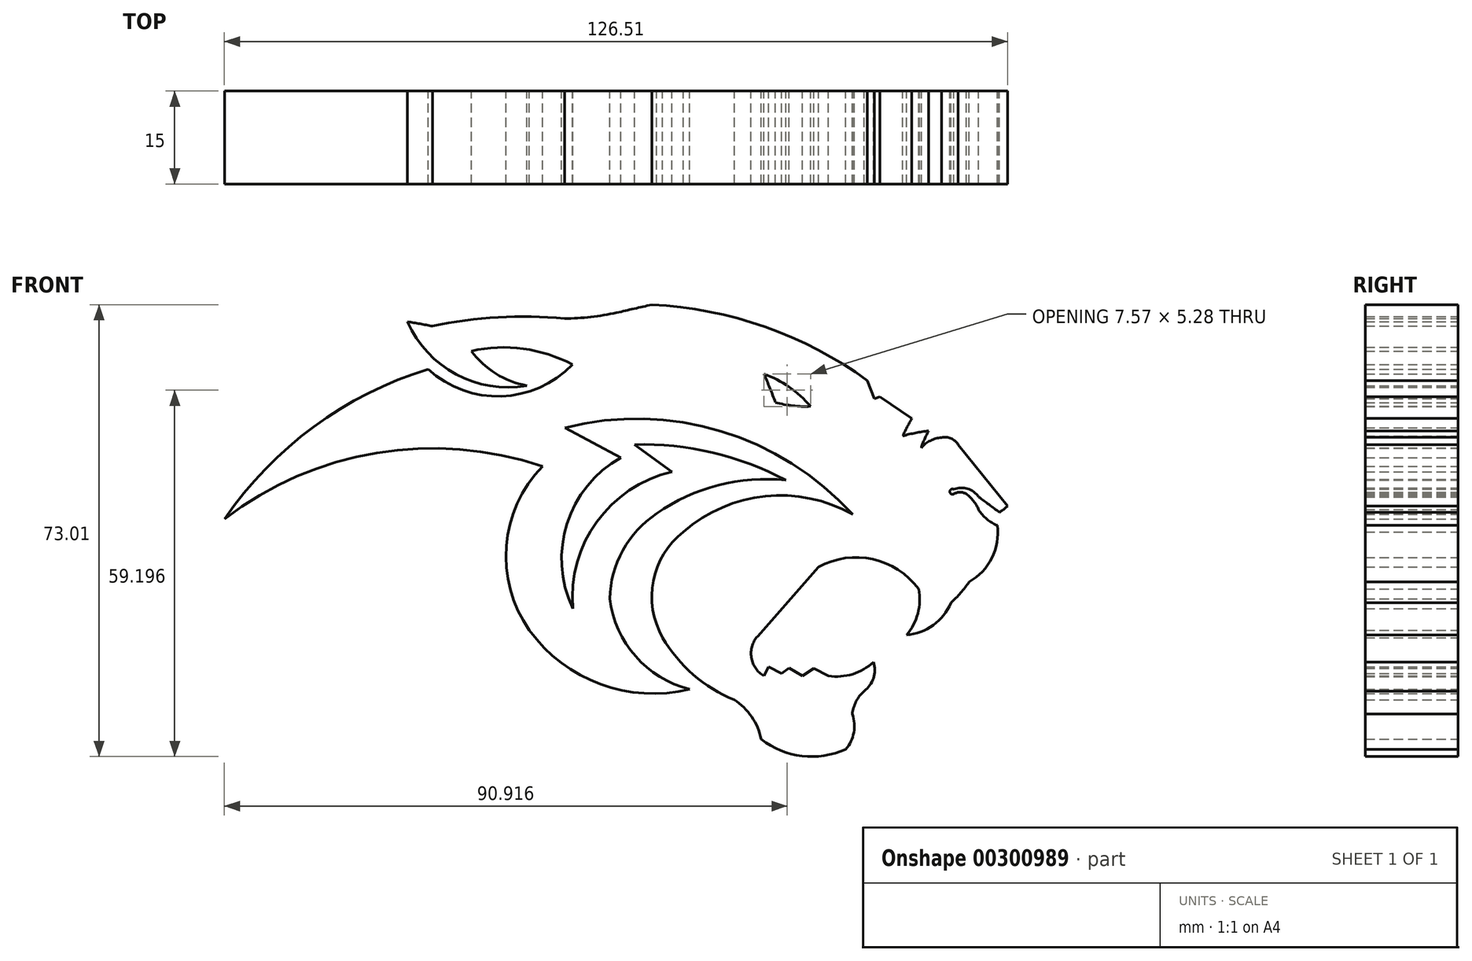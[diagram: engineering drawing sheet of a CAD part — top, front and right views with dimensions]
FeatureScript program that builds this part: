
annotation { "Feature Type Name" : "Feature", "Feature Type Description" : "" }
export const myFeature = defineFeature(function(context is Context, id is Id, definition is map)
    precondition{}
    {
        {
            var Q0;
            Q0=qCreatedBy(makeId("Front.planeOp"),FACE);
            var sketch = newSketch(context, id + "F0", { "sketchPlane" : qUnion([Q0])});
            skArc(sketch, "E0", {"start": v(-29.94, 30.64) * mm, "mid": v(-48.45, 21.32) * mm, "end": v(-62.86, 6.44) * mm});
            skArc(sketch, "E1", {"start": v(-29.94, 30.64) * mm, "mid": v(-18.13, 26.27) * mm, "end": v(-6.62, 31.4) * mm});
            skArc(sketch, "E2", {"start": v(-6.62, 31.4) * mm, "mid": v(-14.6, 33.95) * mm, "end": v(-22.95, 33.58) * mm});
            skArc(sketch, "E3", {"start": v(-22.95, 33.58) * mm, "mid": v(-19, 29.92) * mm, "end": v(-14, 27.98) * mm});
            skArc(sketch, "E4", {"start": v(-33.27, 38.3) * mm, "mid": v(-25.42, 29.8) * mm, "end": v(-14, 27.98) * mm});
            skArc(sketch, "E5", {"start": v(-29.26, 37.6) * mm, "mid": v(-31.26, 37.97) * mm, "end": v(-33.27, 38.3) * mm});
            skArc(sketch, "E6", {"start": v(-7.92, 38.83) * mm, "mid": v(-18.64, 39.04) * mm, "end": v(-29.26, 37.6) * mm});
            skArc(sketch, "E7", {"start": v(-7.92, 38.83) * mm, "mid": v(-3.68, 39.07) * mm, "end": v(0.5, 39.77) * mm});
            skArc(sketch, "E8", {"start": v(0.5, 39.77) * mm, "mid": v(3.34, 40.41) * mm, "end": v(6.17, 41.07) * mm});
            skArc(sketch, "E9", {"start": v(41, 28.8) * mm, "mid": v(24.48, 37.47) * mm, "end": v(6.17, 41.07) * mm});
            skLineSegment(sketch, "E10", {"start": v(41, 28.8) * mm, "end": v(42.13, 25.86) * mm});
            skLineSegment(sketch, "E11", {"start": v(42.13, 25.86) * mm, "end": v(43.05, 26.21) * mm});
            skLineSegment(sketch, "E12", {"start": v(43.05, 26.21) * mm, "end": v(48.2, 22.68) * mm});
            skArc(sketch, "E13", {"start": v(48.2, 22.68) * mm, "mid": v(47.42, 21.29) * mm, "end": v(46.73, 19.85) * mm});
            skArc(sketch, "E14", {"start": v(50.91, 20.67) * mm, "mid": v(48.8, 20.36) * mm, "end": v(46.73, 19.85) * mm});
            skArc(sketch, "E15", {"start": v(50.91, 20.67) * mm, "mid": v(50.25, 19.35) * mm, "end": v(49.73, 17.96) * mm});
            skArc(sketch, "E16", {"start": v(52.98, 19.61) * mm, "mid": v(51.2, 19.1) * mm, "end": v(49.73, 17.96) * mm});
            skArc(sketch, "E17", {"start": v(55.69, 18.43) * mm, "mid": v(54.52, 19.46) * mm, "end": v(52.98, 19.61) * mm});
            skLineSegment(sketch, "E18", {"start": v(55.69, 18.43) * mm, "end": v(63.65, 8.53) * mm});
            skArc(sketch, "E19", {"start": v(62.35, 7.53) * mm, "mid": v(63.03, 8) * mm, "end": v(63.65, 8.53) * mm});
            skArc(sketch, "E20", {"start": v(58.99, 10) * mm, "mid": v(60.67, 8.76) * mm, "end": v(62.35, 7.53) * mm});
            skArc(sketch, "E21", {"start": v(58.99, 10) * mm, "mid": v(57.2, 11.34) * mm, "end": v(54.98, 11.24) * mm});
            skArc(sketch, "E22", {"start": v(54.98, 11.24) * mm, "mid": v(54.32, 10.86) * mm, "end": v(54.98, 10.47) * mm});
            skArc(sketch, "E23", {"start": v(56.99, 10.47) * mm, "mid": v(55.98, 10.77) * mm, "end": v(54.98, 10.47) * mm});
            skArc(sketch, "E24", {"start": v(58.99, 7.94) * mm, "mid": v(58.17, 9.35) * mm, "end": v(56.99, 10.47) * mm});
            skArc(sketch, "E25", {"start": v(58.99, 7.94) * mm, "mid": v(60.3, 6.43) * mm, "end": v(62, 5.4) * mm});
            skArc(sketch, "E26", {"start": v(57.46, -3.73) * mm, "mid": v(61.11, 0.15) * mm, "end": v(62, 5.4) * mm});
            skArc(sketch, "E27", {"start": v(54.5, -7.1) * mm, "mid": v(56.08, -5.5) * mm, "end": v(57.46, -3.73) * mm});
            skLineSegment(sketch, "E28", {"start": v(33.1, -1.32) * mm, "end": v(23.26, -12.52) * mm});
            skArc(sketch, "E29", {"start": v(23.26, -12.52) * mm, "mid": v(22.27, -15.94) * mm, "end": v(24.27, -18.9) * mm});
            skLineSegment(sketch, "E30", {"start": v(24.27, -18.9) * mm, "end": v(25.04, -17.43) * mm});
            skLineSegment(sketch, "E31", {"start": v(25.04, -17.43) * mm, "end": v(27.16, -18.54) * mm});
            skLineSegment(sketch, "E32", {"start": v(27.16, -18.54) * mm, "end": v(28.34, -17.64) * mm});
            skLineSegment(sketch, "E33", {"start": v(28.34, -17.64) * mm, "end": v(30.5, -18.9) * mm});
            skLineSegment(sketch, "E34", {"start": v(30.5, -18.9) * mm, "end": v(32.33, -17.7) * mm});
            skLineSegment(sketch, "E35", {"start": v(32.33, -17.7) * mm, "end": v(34.72, -18.9) * mm});
            skArc(sketch, "E36", {"start": v(34.72, -18.9) * mm, "mid": v(38.62, -18.62) * mm, "end": v(42, -16.66) * mm});
            skArc(sketch, "E37", {"start": v(40.46, -21.35) * mm, "mid": v(42, -19.25) * mm, "end": v(42, -16.66) * mm});
            skArc(sketch, "E38", {"start": v(40.46, -21.35) * mm, "mid": v(39.18, -23.04) * mm, "end": v(38.57, -25.07) * mm});
            skArc(sketch, "E39", {"start": v(37.52, -30.75) * mm, "mid": v(38.82, -28.05) * mm, "end": v(38.57, -25.07) * mm});
            skArc(sketch, "E40", {"start": v(23.85, -29.14) * mm, "mid": v(30.46, -31.85) * mm, "end": v(37.52, -30.75) * mm});
            skArc(sketch, "E41", {"start": v(23.85, -29.14) * mm, "mid": v(22.32, -25.5) * mm, "end": v(19.5, -22.76) * mm});
            skArc(sketch, "E42", {"start": v(38.64, 7.18) * mm, "mid": v(24.53, 10.12) * mm, "end": v(11.3, 4.37) * mm});
            skArc(sketch, "E43", {"start": v(11.3, 4.37) * mm, "mid": v(6.44, -3.55) * mm, "end": v(7.94, -12.73) * mm});
            skArc(sketch, "E44", {"start": v(7.94, -12.73) * mm, "mid": v(12.9, -18.7) * mm, "end": v(19.5, -22.76) * mm});
            skArc(sketch, "E45", {"start": v(38.64, 7.18) * mm, "mid": v(17.34, 20.63) * mm, "end": v(-7.84, 21.2) * mm});
            skLineSegment(sketch, "E46", {"start": v(-7.84, 21.2) * mm, "end": v(1.2, 16.36) * mm});
            skArc(sketch, "E47", {"start": v(1.2, 16.36) * mm, "mid": v(-7.5, 5.7) * mm, "end": v(-6.58, -8.03) * mm});
            skArc(sketch, "E48", {"start": v(9.4, 14.05) * mm, "mid": v(-2.7, 5.99) * mm, "end": v(-6.58, -8.03) * mm});
            skLineSegment(sketch, "E49", {"start": v(9.4, 14.05) * mm, "end": v(3.38, 18.47) * mm});
            skArc(sketch, "E50", {"start": v(27.85, 12.72) * mm, "mid": v(15.98, 17.16) * mm, "end": v(3.38, 18.47) * mm});
            skArc(sketch, "E51", {"start": v(27.85, 12.72) * mm, "mid": v(16.92, 11.9) * mm, "end": v(6.95, 7.32) * mm});
            skArc(sketch, "E52", {"start": v(6.95, 7.32) * mm, "mid": v(1.5, 1.37) * mm, "end": v(-0.62, -6.42) * mm});
            skArc(sketch, "E53", {"start": v(-0.62, -6.42) * mm, "mid": v(3.57, -15.74) * mm, "end": v(12.28, -21.07) * mm});
            skArc(sketch, "E54", {"start": v(-13.59, -11.54) * mm, "mid": v(-2.1, -20.23) * mm, "end": v(12.28, -21.07) * mm});
            skArc(sketch, "E55", {"start": v(-11.48, 14.96) * mm, "mid": v(-17.3, 2.09) * mm, "end": v(-13.59, -11.54) * mm});
            skArc(sketch, "E56", {"start": v(-11.48, 14.96) * mm, "mid": v(-38.23, 17.11) * mm, "end": v(-62.86, 6.44) * mm});
            skArc(sketch, "E57", {"start": v(26.16, 25.27) * mm, "mid": v(25.26, 27.6) * mm, "end": v(24.27, 29.9) * mm});
            skArc(sketch, "E58", {"start": v(26.16, 25.27) * mm, "mid": v(28.98, 24.73) * mm, "end": v(31.84, 24.64) * mm});
            skArc(sketch, "E59", {"start": v(31.84, 24.64) * mm, "mid": v(28.4, 27.75) * mm, "end": v(24.27, 29.9) * mm});
            skArc(sketch, "E60", {"start": v(47.34, -12.31) * mm, "mid": v(51.65, -10.7) * mm, "end": v(54.5, -7.1) * mm});
            skArc(sketch, "E61", {"start": v(47.34, -12.31) * mm, "mid": v(49.17, -8.82) * mm, "end": v(49.3, -4.88) * mm});
            skArc(sketch, "E62", {"start": v(49.3, -4.88) * mm, "mid": v(41.87, -0.06) * mm, "end": v(33.1, -1.32) * mm});
            skSolve(sketch);
        }
        {
            var Q0;
            Q0 = qSketchRegion(id + "F0", true);
            extrude(context, id + "F1", {"entities" : qUnion([Q0]), "offsetDistance" : 25 * mm, "depth" : 15 * mm});
        }
    });
